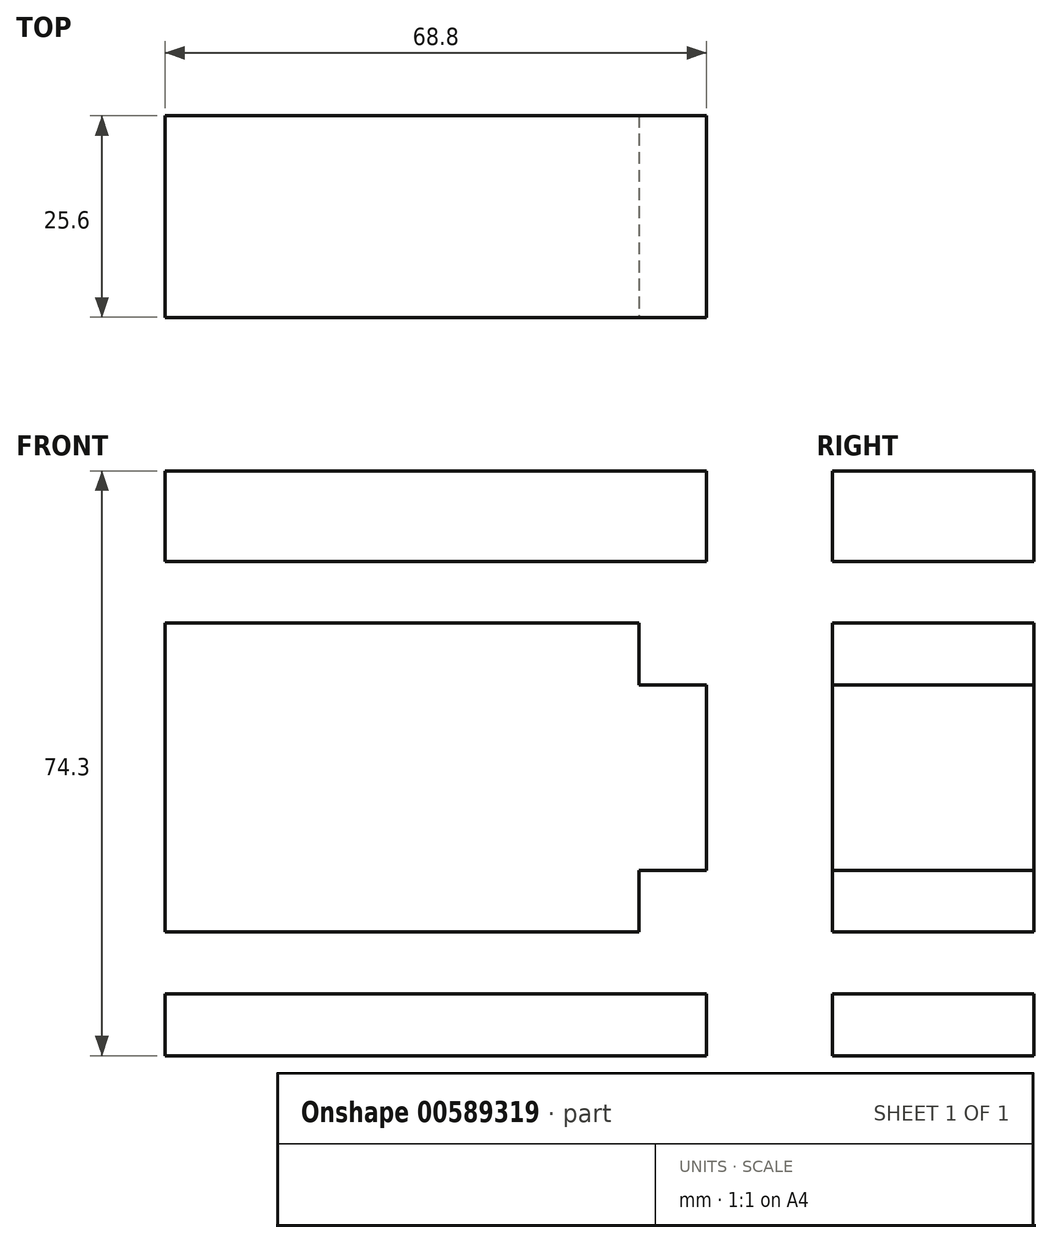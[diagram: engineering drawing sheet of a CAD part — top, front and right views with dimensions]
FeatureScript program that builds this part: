
annotation { "Feature Type Name" : "Feature", "Feature Type Description" : "" }
export const myFeature = defineFeature(function(context is Context, id is Id, definition is map)
    precondition{}
    {
        {
            var Q0;
            Q0=qCreatedBy(makeId("Top.planeOp"),FACE);
            var sketch = newSketch(context, id + "F0", { "sketchPlane" : qUnion([Q0])});
            skLineSegment(sketch, "E0.bottom", {"start": v(-34.4, 12.8) * mm, "end": v(34.4, 12.8) * mm});
            skLineSegment(sketch, "E0.top", {"start": v(-34.4, -12.8) * mm, "end": v(34.4, -12.8) * mm});
            skLineSegment(sketch, "E0.left", {"start": v(-34.4, 12.8) * mm, "end": v(-34.4, -12.8) * mm});
            skLineSegment(sketch, "E0.right", {"start": v(34.4, 12.8) * mm, "end": v(34.4, -12.8) * mm});
            skPoint(sketch, "E0.middle", {"position": v(0, 0) * mm});
            skSolve(sketch);
        }
        {
            var Q0;
            Q0=makeQuery(id+"F0.imprint","IMPRINT",FACE,{"disambiguationData":[TD([[makeQuery(id+"F0.imprint","IMPRINT",EDGE,{"derivedFrom":sQuery(id+"F0.wireOp",EDGE,"E0.bottom")}),-1.0]])]});
            extrude(context, id + "F1", {"entities" : qUnion([Q0]), "depth" : 25.6 * mm, "offsetDistance" : 25.4 * mm});
        }
        {
            var Q0;
            Q0=makeQuery(id+"F1.opExtrude","CAP_FACE",FACE,{"disambiguationData":[OSD([sQuery(id+"F0.wireOp",EDGE,"E0.bottom"),sQuery(id+"F0.wireOp",EDGE,"E0.top"),sQuery(id+"F0.wireOp",EDGE,"E0.left"),sQuery(id+"F0.wireOp",EDGE,"E0.right")])],"isStart":true});
            extrude(context, id + "F2", {"entities" : qUnion([Q0]), "operationType" : NewBodyOperationType.ADD, "depth" : 100 * mm, "offsetDistance" : 25.4 * mm});
        }
        {
            var Q0;
            {var subQ0=sQuery(id+"F0.wireOp",EDGE,"E0.top");Q0=makeQuery(id+"F2.boolean.opBoolean","MERGE",FACE,{"derivedFrom":[makeQuery(id+"F1.opExtrude","SWEPT_FACE",FACE,{"disambiguationData":[OSD([subQ0])]}),makeQuery(id+"F2.opExtrude","SWEPT_FACE",FACE,{"disambiguationData":[OSD([subQ0])]})]});}
            var sketch = newSketch(context, id + "F3", { "sketchPlane" : qUnion([Q0])});
            skLineSegment(sketch, "E1", {"start": v(0, 25.6) * mm, "end": v(0, -100) * mm});
            skLineSegment(sketch, "E2", {"start": v(0, -100) * mm, "end": v(0, -37.2) * mm});
            skLineSegment(sketch, "E3", {"start": v(0, -37.2) * mm, "end": v(34.4, -37.2) * mm});
            skLineSegment(sketch, "E4", {"start": v(34.4, -37.2) * mm, "end": v(-34.4, -37.2) * mm});
            skLineSegment(sketch, "E5", {"start": v(-34.4, -37.2) * mm, "end": v(-34.4, -100) * mm});
            skLineSegment(sketch, "E6", {"start": v(-34.4, -100) * mm, "end": v(0, -100) * mm});
            skLineSegment(sketch, "E7", {"start": v(-17.2, -100) * mm, "end": v(-17.2, -37.2) * mm});
            skLineSegment(sketch, "E8", {"start": v(-17.2, -37.2) * mm, "end": v(0, -37.2) * mm});
            skLineSegment(sketch, "E9", {"start": v(0, -68.6) * mm, "end": v(-34.4, -68.6) * mm});
            skLineSegment(sketch, "E10", {"start": v(-34.4, -68.6) * mm, "end": v(-17.2, -68.6) * mm});
            skLineSegment(sketch, "E11", {"start": v(-17.2, -68.6) * mm, "end": v(-17.2, -100) * mm});
            skLineSegment(sketch, "E12", {"start": v(0, -68.6) * mm, "end": v(34.4, -68.6) * mm});
            skLineSegment(sketch, "E13", {"start": v(34.4, -68.6) * mm, "end": v(17.2, -68.6) * mm});
            skLineSegment(sketch, "E14", {"start": v(17.2, -68.6) * mm, "end": v(17.2, -100) * mm});
            skLineSegment(sketch, "E15", {"start": v(17.2, -100) * mm, "end": v(17.2, -37.2) * mm});
            skLineSegment(sketch, "E16", {"start": v(17.2, -37.2) * mm, "end": v(17.2, -84.3) * mm});
            skLineSegment(sketch, "E17", {"start": v(17.2, -84.3) * mm, "end": v(34.4, -84.3) * mm});
            skLineSegment(sketch, "E18", {"start": v(17.2, -84.3) * mm, "end": v(-34.4, -84.3) * mm});
            skLineSegment(sketch, "E19", {"start": v(-34.4, -84.3) * mm, "end": v(-34.4, -68.6) * mm});
            skLineSegment(sketch, "E20", {"start": v(-25.8, -68.6) * mm, "end": v(-25.8, -100) * mm});
            skLineSegment(sketch, "E21", {"start": v(-25.8, -100) * mm, "end": v(-17.2, -100) * mm});
            skLineSegment(sketch, "E22", {"start": v(-8.6, -84.3) * mm, "end": v(-8.6, -100) * mm});
            skLineSegment(sketch, "E23", {"start": v(-8.6, -100) * mm, "end": v(-8.6, -68.6) * mm});
            skLineSegment(sketch, "E24", {"start": v(-8.6, -68.6) * mm, "end": v(0, -68.6) * mm});
            skLineSegment(sketch, "E25", {"start": v(25.8, -84.3) * mm, "end": v(25.8, -68.6) * mm});
            skLineSegment(sketch, "E26", {"start": v(25.8, -68.6) * mm, "end": v(0, -68.6) * mm});
            skLineSegment(sketch, "E27", {"start": v(0, -84.3) * mm, "end": v(17.2, -84.3) * mm});
            skLineSegment(sketch, "E28", {"start": v(17.2, -68.6) * mm, "end": v(0, -68.6) * mm});
            skLineSegment(sketch, "E29", {"start": v(8.6, -84.3) * mm, "end": v(8.6, -68.6) * mm});
            skLineSegment(sketch, "E30", {"start": v(8.6, -68.6) * mm, "end": v(17.2, -68.6) * mm});
            skLineSegment(sketch, "E31", {"start": v(8.6, -76.45) * mm, "end": v(0, -76.45) * mm});
            skLineSegment(sketch, "E32", {"start": v(0, -76.45) * mm, "end": v(17.2, -76.45) * mm});
            skLineSegment(sketch, "E33", {"start": v(17.2, -76.45) * mm, "end": v(34.4, -76.45) * mm});
            skLineSegment(sketch, "E34", {"start": v(34.4, -76.45) * mm, "end": v(-34.4, -76.45) * mm});
            skLineSegment(sketch, "E35", {"start": v(-34.4, -76.45) * mm, "end": v(-34.4, -84.3) * mm});
            skLineSegment(sketch, "E36", {"start": v(-25.8, -84.3) * mm, "end": v(-25.8, -100) * mm});
            skLineSegment(sketch, "E37", {"start": v(-34.4, -100) * mm, "end": v(-34.4, -84.3) * mm});
            skLineSegment(sketch, "E38", {"start": v(-34.4, -92.15) * mm, "end": v(34.4, -92.15) * mm});
            skLineSegment(sketch, "E39", {"start": v(25.8, -100) * mm, "end": v(25.8, -84.3) * mm});
            skLineSegment(sketch, "E40", {"start": v(8.6, -84.3) * mm, "end": v(8.6, -100) * mm});
            skLineSegment(sketch, "E41", {"start": v(-25.8, -68.6) * mm, "end": v(-25.8, 25.6) * mm});
            skLineSegment(sketch, "E42", {"start": v(-8.6, -68.6) * mm, "end": v(-8.6, 25.6) * mm});
            skLineSegment(sketch, "E43", {"start": v(8.6, -68.6) * mm, "end": v(8.6, 25.6) * mm});
            skLineSegment(sketch, "E44", {"start": v(25.8, -68.6) * mm, "end": v(25.8, 25.6) * mm});
            skLineSegment(sketch, "E45", {"start": v(17.2, -37.2) * mm, "end": v(17.2, 25.6) * mm});
            skLineSegment(sketch, "E46", {"start": v(-17.2, -37.2) * mm, "end": v(-17.2, 25.6) * mm});
            skLineSegment(sketch, "E47", {"start": v(-34.4, -37.2) * mm, "end": v(-34.4, -68.6) * mm});
            skLineSegment(sketch, "E48", {"start": v(-25.8, -68.6) * mm, "end": v(-25.8, -37.2) * mm});
            skLineSegment(sketch, "E49", {"start": v(-25.8, -37.2) * mm, "end": v(-25.8, -52.9) * mm});
            skLineSegment(sketch, "E50", {"start": v(-25.8, -52.9) * mm, "end": v(-34.4, -52.9) * mm});
            skLineSegment(sketch, "E51", {"start": v(-34.4, -52.9) * mm, "end": v(34.4, -52.9) * mm});
            skLineSegment(sketch, "E52", {"start": v(-34.4, -52.9) * mm, "end": v(-25.8, -52.9) * mm});
            skLineSegment(sketch, "E53", {"start": v(-25.8, -52.9) * mm, "end": v(-25.8, -68.6) * mm});
            skLineSegment(sketch, "E54", {"start": v(-25.8, -60.75) * mm, "end": v(-34.4, -60.75) * mm});
            skPoint(sketch, "E54.endSnap0", {"position": v(-30.1, -60.75) * mm});
            skLineSegment(sketch, "E55", {"start": v(-25.8, -60.75) * mm, "end": v(34.4, -60.75) * mm});
            skLineSegment(sketch, "E56", {"start": v(-34.4, -37.2) * mm, "end": v(-34.4, -52.9) * mm});
            skLineSegment(sketch, "E57", {"start": v(-34.4, -45.05) * mm, "end": v(34.4, -45.05) * mm});
            skSolve(sketch);
        }
        {
            var Q0;
            {var subQ0=sQuery(id+"F3.wireOp",EDGE,"E37");var subQ5=sQuery(id+"F3.wireOp",EDGE,"E38");var subQ6=makeQuery(id+"F3.imprint","INTERSECT",VERTEX,{"derivedFrom":[subQ0,subQ5]});Q0=makeQuery(id+"F3.imprint","IMPRINT",FACE,{"disambiguationData":[TD([[makeQuery(id+"F3.imprint","IMPRINT",EDGE,{"disambiguationData":[TD([[subQ6,-1.0]])],"derivedFrom":subQ5}),1.0]])]});}
            var Q1;
            {var subQ0=sQuery(id+"F3.wireOp",EDGE,"E19");Q1=makeQuery(id+"F3.imprint","IMPRINT",FACE,{"disambiguationData":[TD([[makeQuery(id+"F3.imprint","IMPRINT",EDGE,{"derivedFrom":subQ0}),1.0]])]});}
            var Q2;
            {var subQ0=sQuery(id+"F3.wireOp",EDGE,"E52");Q2=makeQuery(id+"F3.imprint","IMPRINT",FACE,{"disambiguationData":[TD([[makeQuery(id+"F3.imprint","IMPRINT",EDGE,{"derivedFrom":subQ0}),-1.0]])]});}
            var Q3;
            {var subQ0=sQuery(id+"F3.wireOp",EDGE,"E56");var subQ7=sQuery(id+"F3.wireOp",EDGE,"E57");var subQ9=makeQuery(id+"F3.imprint","INTERSECT",VERTEX,{"derivedFrom":[subQ0,subQ7]});Q3=makeQuery(id+"F3.imprint","IMPRINT",FACE,{"disambiguationData":[TD([[makeQuery(id+"F3.imprint","IMPRINT",EDGE,{"disambiguationData":[TD([[subQ9,-1.0]])],"derivedFrom":subQ7}),1.0]])]});}
            var Q4;
            {var subQ5=sQuery(id+"F3.wireOp",EDGE,"E25");var subQ7=sQuery(id+"F3.wireOp",EDGE,"E34");var subQ8=makeQuery(id+"F3.imprint","INTERSECT",VERTEX,{"derivedFrom":[subQ5,subQ7]});Q4=makeQuery(id+"F3.imprint","IMPRINT",FACE,{"disambiguationData":[TD([[makeQuery(id+"F3.imprint","IMPRINT",EDGE,{"disambiguationData":[TD([[subQ8,1.0]])],"derivedFrom":subQ5}),-1.0]])]});}
            var Q5;
            {var subQ0=sQuery(id+"F3.wireOp",EDGE,"E13");Q5=makeQuery(id+"F3.imprint","IMPRINT",FACE,{"disambiguationData":[TD([[makeQuery(id+"F3.imprint","IMPRINT",EDGE,{"derivedFrom":subQ0}),-1.0]])]});}
            var Q6;
            {var subQ0=sQuery(id+"F3.wireOp",EDGE,"E51");var subQ1=sQuery(id+"F3.wireOp",EDGE,"E44");var subQ2=makeQuery(id+"F3.imprint","INTERSECT",VERTEX,{"derivedFrom":[subQ1,subQ0]});Q6=makeQuery(id+"F3.imprint","IMPRINT",FACE,{"disambiguationData":[TD([[makeQuery(id+"F3.imprint","IMPRINT",EDGE,{"disambiguationData":[TD([[subQ2,-1.0]])],"derivedFrom":subQ1}),-1.0]])]});}
            extrude(context, id + "F4", {"entities" : qUnion([Q0, Q1, Q2, Q3, Q4, Q5, Q6]), "operationType" : NewBodyOperationType.REMOVE, "oppositeDirection" : true, "depth" : 50 * mm, "offsetDistance" : 25.4 * mm});
        }
        {
            var Q0;
            Q0=makeQuery(id+"F1.opExtrude","CAP_FACE",FACE,{"disambiguationData":[OSD([sQuery(id+"F0.wireOp",EDGE,"E0.bottom"),sQuery(id+"F0.wireOp",EDGE,"E0.top"),sQuery(id+"F0.wireOp",EDGE,"E0.left"),sQuery(id+"F0.wireOp",EDGE,"E0.right")])],"isStart":false});
            extrude(context, id + "F5", {"entities" : qUnion([Q0]), "operationType" : NewBodyOperationType.REMOVE, "oppositeDirection" : true, "depth" : 51.3 * mm, "offsetDistance" : 25.4 * mm});
        }
    });
